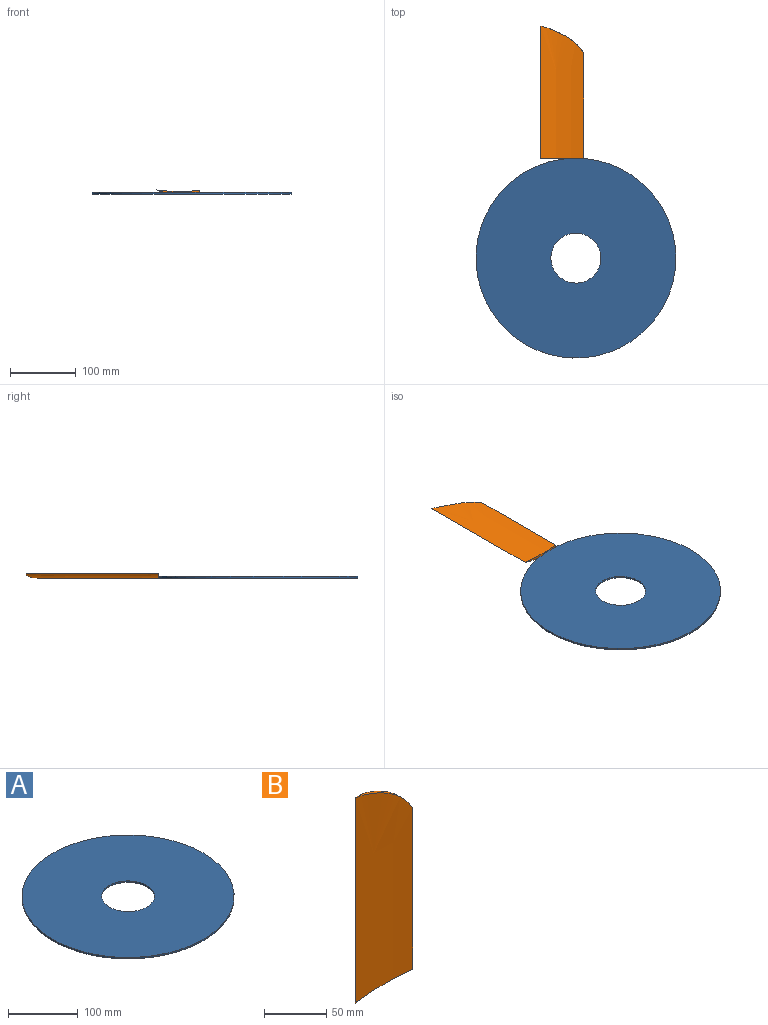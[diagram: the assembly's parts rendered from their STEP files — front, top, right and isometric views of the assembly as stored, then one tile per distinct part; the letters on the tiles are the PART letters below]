
ASSEMBLY  parts=2 mates=1
PART A: 4 faces, bbox 304.8x304.8x2.5 mm
  f0: cylinder r=38.1mm len=76.2mm, axis (0,0,-1), area 608mm2, adj f2,f3
  f1: cylinder r=152.4mm len=304.8mm, axis (0,0,-1), area 2432.2mm2, adj f2,f3
  f2: plane 304.8x304.8mm, normal (0,0,1), area 68405.5mm2, adj f0,f1
  f3: plane 304.8x304.8mm, normal (0,0,-1), area 68405.5mm2, adj f0,f1
PART B: 6 faces, bbox 66.3x6.9x201.6 mm
  f0: plane 159.07x5.52mm, normal (1,0,0), area 877.8mm2, adj f1,f3,f4,f5
  f1: plane 184.5x25.46mm, normal (0,1,0), area 4286.2mm2, adj f0,f2,f4,f5
  f2: extruded ~201.57x41.25mm, area 8149.8mm2, adj f1,f3,f4,f5
  f3: extruded ~201.57x65.93mm, area 12325.7mm2, adj f0,f2,f4,f5
  f4: plane 65.93x6.88mm, normal (0,0,-1), area 222mm2, adj f0,f1,f2,f3
  f5: extruded ~65.93x42.5mm, area 285.5mm2, adj f0,f1,f2,f3
PLACE A t=(-49.56,-32.1,-16.05)mm
PLACE B rot(axis=(-1,0,0),90deg) t=(-47.45,120.3,33.54)mm
MATE fastened B.f1 <-> A.f3  axis (0,0,-1) through (-49.56,120.3,-16.05)mm
